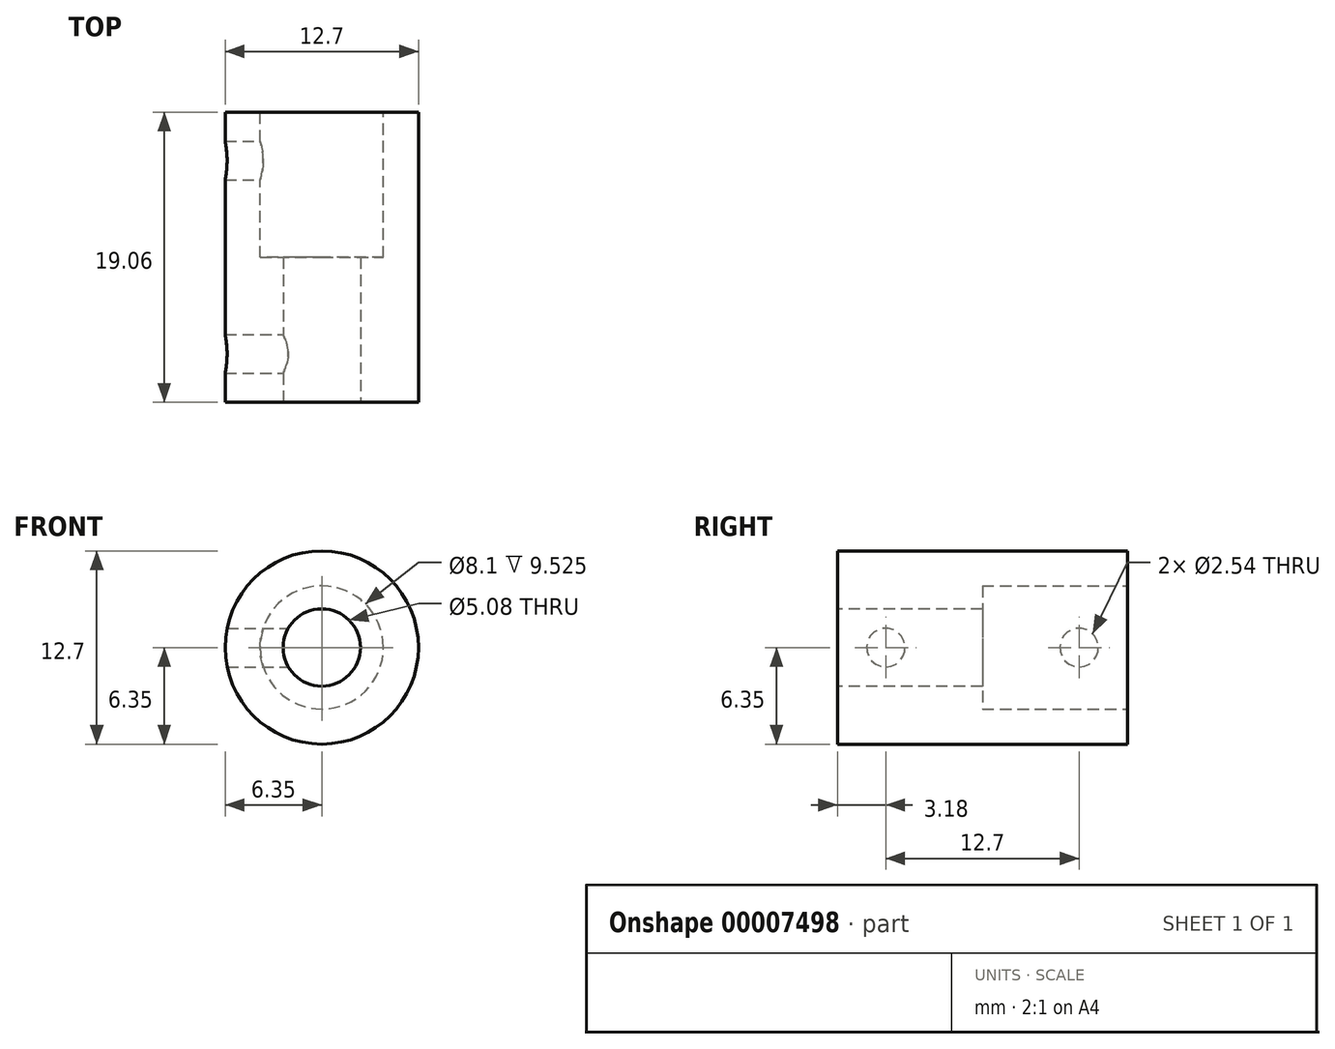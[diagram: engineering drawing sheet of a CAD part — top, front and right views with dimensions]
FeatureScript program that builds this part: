
annotation { "Feature Type Name" : "Feature", "Feature Type Description" : "" }
export const myFeature = defineFeature(function(context is Context, id is Id, definition is map)
    precondition{}
    {
        {
            var Q0;
            Q0=qCreatedBy(makeId("Front.planeOp"),FACE);
            var sketch = newSketch(context, id + "F0", { "sketchPlane" : qUnion([Q0])});
            skCircle(sketch, "E0", {"center": v(0, 0) * mm, "radius": 6.35 * mm});
            skSolve(sketch);
        }
        {
            var Q0;
            Q0 = qSketchRegion(id + "F0", true);
            extrude(context, id + "F1", {"entities" : qUnion([Q0]), "endBound" : BoundingType.SYMMETRIC, "depth" : 19.05 * mm});
        }
        {
            var Q0;
            Q0=makeQuery(id+"F1.opExtrude","CAP_FACE",FACE,{"disambiguationData":[OSD([sQuery(id+"F0.wireOp",EDGE,"E0")])],"isStart":true});
            var sketch = newSketch(context, id + "F2", { "sketchPlane" : qUnion([Q0])});
            skCircle(sketch, "E1", {"center": v(0, 0) * mm, "radius": 4.05 * mm});
            skSolve(sketch);
        }
        {
            var Q0;
            Q0 = qSketchRegion(id + "F2", true);
            extrude(context, id + "F3", {"entities" : qUnion([Q0]), "operationType" : NewBodyOperationType.REMOVE, "oppositeDirection" : true, "depth" : 9.52 * mm});
        }
        {
            var Q0;
            Q0=makeQuery(id+"F1.opExtrude","CAP_FACE",FACE,{"disambiguationData":[OSD([sQuery(id+"F0.wireOp",EDGE,"E0")])],"isStart":false});
            var sketch = newSketch(context, id + "F4", { "sketchPlane" : qUnion([Q0])});
            skCircle(sketch, "E2", {"center": v(0, 0) * mm, "radius": 2.54 * mm});
            skSolve(sketch);
        }
        {
            var Q0;
            Q0 = qSketchRegion(id + "F4", true);
            extrude(context, id + "F5", {"entities" : qUnion([Q0]), "operationType" : NewBodyOperationType.REMOVE, "endBound" : BoundingType.THROUGH_ALL, "oppositeDirection" : true, "depth" : 25.4 * mm});
        }
        {
            var Q0;
            Q0=qCreatedBy(makeId("Right.planeOp"),FACE);
            var sketch = newSketch(context, id + "F6", { "sketchPlane" : qUnion([Q0])});
            skCircle(sketch, "E3", {"center": v(-6.35, 0) * mm, "radius": 1.27 * mm});
            skCircle(sketch, "E4", {"center": v(6.35, 0) * mm, "radius": 1.27 * mm});
            skLineSegment(sketch, "E5", {"start": v(0, 0) * mm, "end": v(0, 12.8) * mm, "construction": true});
            skSolve(sketch);
        }
        {
            var Q0;
            Q0=makeQuery(id+"F6.imprint","IMPRINT",FACE,{"disambiguationData":[TD([[makeQuery(id+"F6.imprint","IMPRINT",EDGE,{"derivedFrom":sQuery(id+"F6.wireOp",EDGE,"E4")}),1.0]])]});
            var Q1;
            Q1=makeQuery(id+"F6.imprint","IMPRINT",FACE,{"disambiguationData":[TD([[makeQuery(id+"F6.imprint","IMPRINT",EDGE,{"derivedFrom":sQuery(id+"F6.wireOp",EDGE,"E3")}),1.0]])]});
            extrude(context, id + "F7", {"entities" : qUnion([Q0, Q1]), "operationType" : NewBodyOperationType.REMOVE, "oppositeDirection" : true, "depth" : 25.4 * mm});
        }
    });
